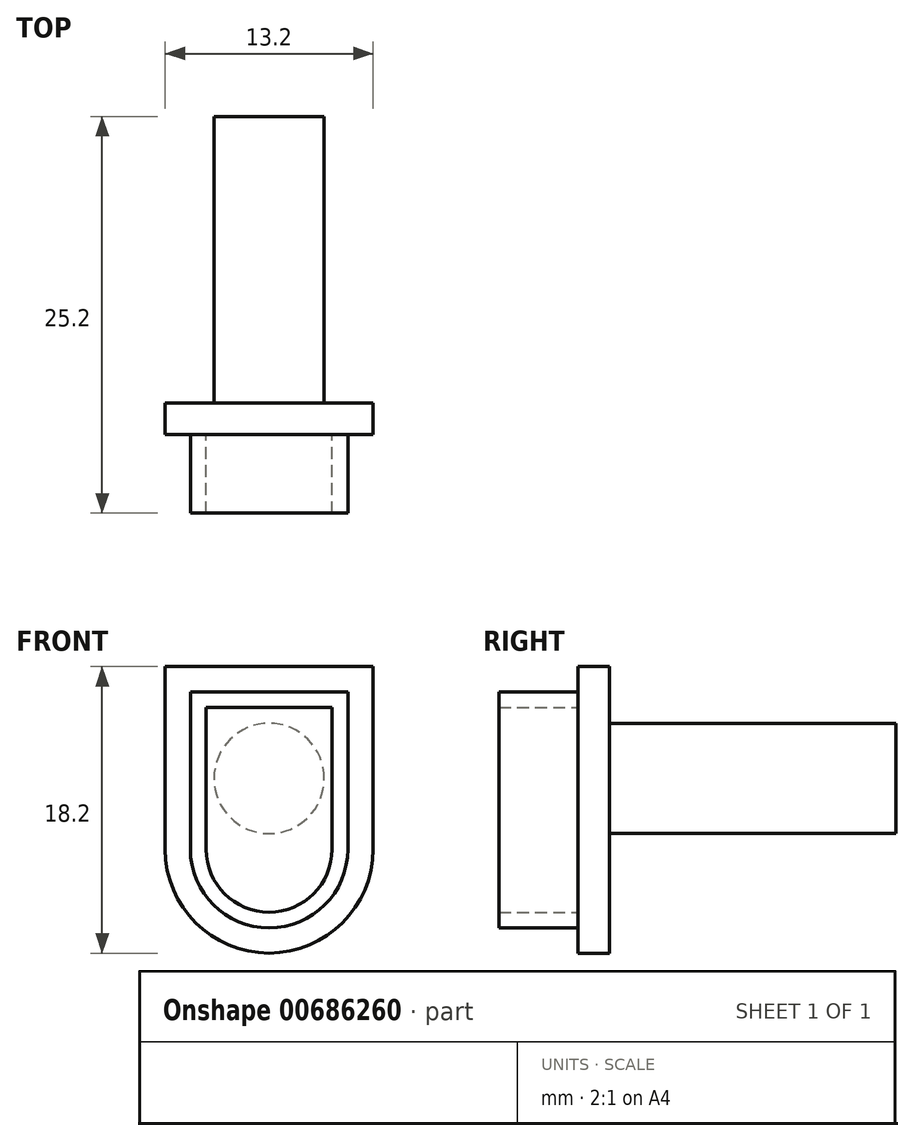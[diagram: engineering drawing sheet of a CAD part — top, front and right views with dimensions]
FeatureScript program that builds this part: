
annotation { "Feature Type Name" : "Feature", "Feature Type Description" : "" }
export const myFeature = defineFeature(function(context is Context, id is Id, definition is map)
    precondition{}
    {
        {
            var Q0;
            Q0=qCreatedBy(makeId("Front.planeOp"),FACE);
            var sketch = newSketch(context, id + "F0", { "sketchPlane" : qUnion([Q0])});
            skLineSegment(sketch, "E0.bottom", {"start": v(-24.01, 18.82) * mm, "end": v(-14.01, 18.82) * mm});
            skLineSegment(sketch, "E0.left", {"start": v(-24.01, 18.82) * mm, "end": v(-24.01, 8.82) * mm});
            skLineSegment(sketch, "E0.right", {"start": v(-14.01, 18.82) * mm, "end": v(-14.01, 8.82) * mm});
            skArc(sketch, "E1", {"start": v(-24.01, 8.82) * mm, "mid": v(-19.01, 3.82) * mm, "end": v(-14.01, 8.82) * mm});
            skLineSegment(sketch, "E2.0", {"start": v(-23.01, 17.82) * mm, "end": v(-15.01, 17.82) * mm});
            skLineSegment(sketch, "E2.1", {"start": v(-23.01, 17.82) * mm, "end": v(-23.01, 8.82) * mm});
            skArc(sketch, "E2.2", {"start": v(-23.01, 8.82) * mm, "mid": v(-19.01, 4.82) * mm, "end": v(-15.01, 8.82) * mm});
            skLineSegment(sketch, "E2.3", {"start": v(-15.01, 17.82) * mm, "end": v(-15.01, 8.82) * mm});
            skLineSegment(sketch, "E3.0", {"start": v(-25.61, 20.42) * mm, "end": v(-12.41, 20.42) * mm});
            skLineSegment(sketch, "E3.1", {"start": v(-25.61, 20.42) * mm, "end": v(-25.61, 8.82) * mm});
            skArc(sketch, "E3.2", {"start": v(-25.61, 8.82) * mm, "mid": v(-19.01, 2.22) * mm, "end": v(-12.41, 8.82) * mm});
            skLineSegment(sketch, "E3.3", {"start": v(-12.41, 20.42) * mm, "end": v(-12.41, 8.82) * mm});
            skCircle(sketch, "E4", {"center": v(-19.01, 13.32) * mm, "radius": 3.5 * mm});
            skPoint(sketch, "E4.centerSnap0", {"position": v(-15.01, 13.32) * mm});
            skSolve(sketch);
        }
        {
            var Q0;
            Q0=makeQuery(id+"F0.imprint","IMPRINT",FACE,{"disambiguationData":[TD([[makeQuery(id+"F0.imprint","IMPRINT",EDGE,{"derivedFrom":sQuery(id+"F0.wireOp",EDGE,"E0.bottom")}),-1.0]])]});
            var Q1;
            Q1=makeQuery(id+"F0.imprint","IMPRINT",FACE,{"disambiguationData":[TD([[makeQuery(id+"F0.imprint","IMPRINT",EDGE,{"derivedFrom":sQuery(id+"F0.wireOp",EDGE,"E0.bottom")}),1.0]])]});
            var Q2;
            Q2=makeQuery(id+"F0.imprint","IMPRINT",FACE,{"disambiguationData":[TD([[makeQuery(id+"F0.imprint","IMPRINT",EDGE,{"derivedFrom":sQuery(id+"F0.wireOp",EDGE,"E2.0")}),-1.0]])]});
            extrude(context, id + "F1", {"entities" : qUnion([Q0, Q1, Q2]), "oppositeDirection" : true, "depth" : 2 * mm, "offsetDistance" : 25 * mm});
        }
        {
            var Q0;
            Q0=makeQuery(id+"F0.imprint","IMPRINT",FACE,{"disambiguationData":[TD([[makeQuery(id+"F0.imprint","IMPRINT",EDGE,{"derivedFrom":sQuery(id+"F0.wireOp",EDGE,"E0.bottom")}),-1.0]])]});
            extrude(context, id + "F2", {"entities" : qUnion([Q0]), "operationType" : NewBodyOperationType.ADD, "depth" : 5 * mm, "offsetDistance" : 25 * mm});
        }
        {
            var Q0;
            Q0=makeQuery(id+"F0.imprint","IMPRINT",FACE,{"disambiguationData":[TD([[makeQuery(id+"F0.imprint","IMPRINT",EDGE,{"derivedFrom":sQuery(id+"F0.wireOp",EDGE,"E4")}),1.0]])]});
            extrude(context, id + "F3", {"entities" : qUnion([Q0]), "operationType" : NewBodyOperationType.ADD, "oppositeDirection" : true, "depth" : 20.2 * mm, "offsetDistance" : 25 * mm});
        }
    });
